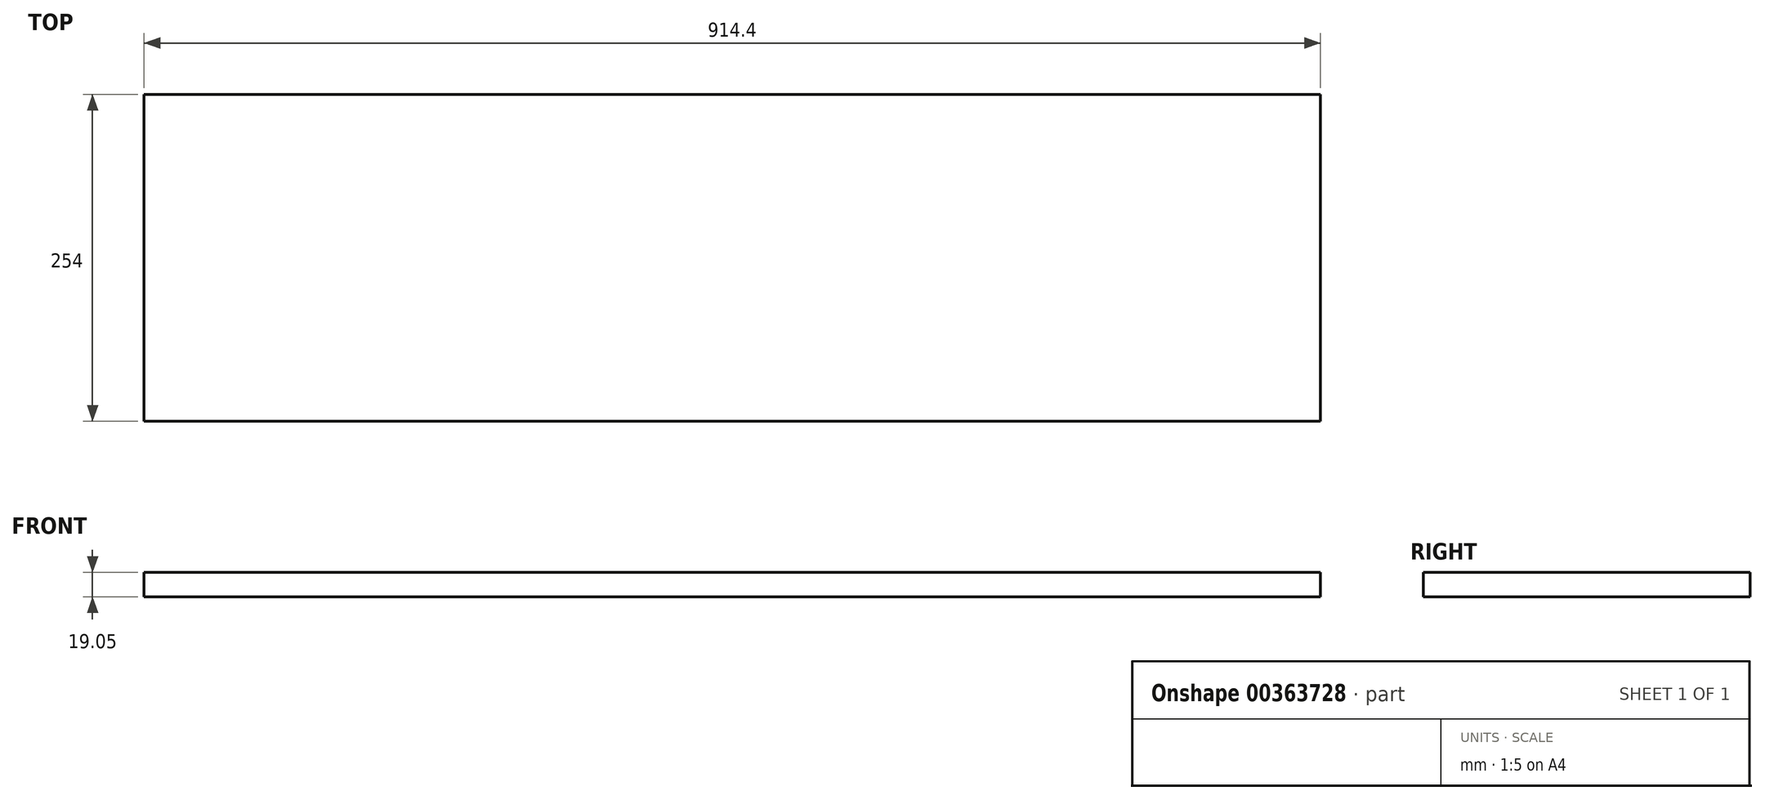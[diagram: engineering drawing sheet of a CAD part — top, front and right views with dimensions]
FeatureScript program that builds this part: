
annotation { "Feature Type Name" : "Feature", "Feature Type Description" : "" }
export const myFeature = defineFeature(function(context is Context, id is Id, definition is map)
    precondition{}
    {
        {
            var Q0;
            Q0=qCreatedBy(makeId("Top.planeOp"),FACE);
            var sketch = newSketch(context, id + "F0", { "sketchPlane" : qUnion([Q0])});
            skLineSegment(sketch, "E0.bottom", {"start": v(457.2, 127) * mm, "end": v(-457.2, 127) * mm});
            skLineSegment(sketch, "E0.top", {"start": v(457.2, -127) * mm, "end": v(-457.2, -127) * mm});
            skLineSegment(sketch, "E0.left", {"start": v(457.2, 127) * mm, "end": v(457.2, -127) * mm});
            skLineSegment(sketch, "E0.right", {"start": v(-457.2, 127) * mm, "end": v(-457.2, -127) * mm});
            skPoint(sketch, "E0.middle", {"position": v(0, 0) * mm});
            skSolve(sketch);
        }
        {
            var Q0;
            Q0 = qSketchRegion(id + "F0", true);
            var Q1;
            Q1=makeQuery(id+"F0.imprint","IMPRINT",FACE,{"disambiguationData":[TD([[makeQuery(id+"F0.imprint","IMPRINT",EDGE,{"derivedFrom":sQuery(id+"F0.wireOp",EDGE,"E0.bottom")}),1.0]])]});
            extrude(context, id + "F1", {"entities" : qUnion([Q0, Q1]), "offsetDistance" : 25.4 * mm, "depth" : 19.05 * mm});
        }
    });
